# Revit family: M_Ryterna_TL STD
name_source: partatom
category: Doors
revit_build: Autodesk Revit 2018 (Build: 20190510_1515(x64)
units: mm (PartAtom-declared; Revit-internal decimal feet)

## family parameters
Always vertical = Yes
Cut with Voids When Loaded = No
Host = Wall
OmniClass Number = 23.30.10.00
OmniClass Title = Doors
Room Calculation Point = No
Shared = No

## types (1)
- TL STD H3000W3000
    Bottom Gasket Material = Gasket Rubber, Black
    Clearance Zone = Yes
    Door Bottom Offset = 30 mm  [stored 0.0984252 ft]
    Door Height = 2980 mm
    Door Inset = 15 mm  [stored 0.0492126 ft]
    Door Type Color Material = M_Garage Door : RAL 9016/RAL 9002
    Guide Track Material = Steel, Galvanized
    Height = 3000 mm  [stored 9.84252 ft]
    Height_True = 3000 mm  [stored 9.84252 ft]
    Holder Back Distance = 2060 mm  [stored 6.75853 ft]
    Horizontal C Track Material = Steel, Galvanized
    Horizontal Track Length = 1200 mm  [stored 3.93701 ft]
    Lifting Type = M_Lifting Assembly : 0
    Lifting Type A = M_Lifting Assembly : 0
    Lifting Type B = M_Lifting Assembly : 1
    Lifting Type C = M_Lifting Assembly : 2
    Manufacturer = UAB “RYTERNA GROUP”
    Power Operator = No
    Power Operator Material = Steel, Galvanized
    Power Operator Position = 4000 mm  [stored 13.1234 ft]
    Reel Material = Steel, Galvanized
    Rod Material = Steel, Galvanized
    Roller Holder Material = Steel, Galvanized
    Rough Height = 3010 mm  [stored 9.87533 ft]
    Rough Width = 3040 mm  [stored 9.97375 ft]
    Slab Slope = 0.00°
    Slab Slope_True = 0.00°
    Spring Holder Material = Steel, Galvanized
    Spring Material = Steel, Galvanized
    Thickness = 40 mm  [stored 0.131234 ft]
    Top Connection Number = 3
    Top Connection Spacing = 1087 mm
    Top Gasket Material = Gasket Rubber, Black
    Triangle Connection Material = Steel, Galvanized
    URL = https://www.ryterna.eu
    Vertical L Profile Material = Steel, Galvanized
    Wall Closure = By host
    Warning Message = No
    Width = 3000 mm  [stored 9.84252 ft]
    Width_True = 3000 mm  [stored 9.84252 ft]
    Zone A Vertical Distance = 310 mm  [stored 1.01706 ft]
    Zone B Horizontal Distance = 617 mm
    Zone B Vertical Distance = 107 mm
    Zone Sloped Thickness = 30 mm  [stored 0.0984252 ft]
    Zone Vertical Thickness = 155 mm  [stored 0.50853 ft]
    h = 341 mm  [stored 1.11877 ft]

note: [stored X ft] marks values corroborated as IEEE doubles in the binary element streams (Revit-internal decimal feet)

## geometry (parser evidence)
native form markers: Blend x6, Sweep x82
no freeform markers — native parametric forms only
